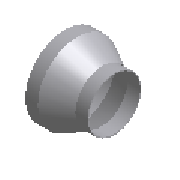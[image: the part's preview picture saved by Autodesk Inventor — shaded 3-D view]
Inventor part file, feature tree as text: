
AUTODESK INVENTOR PART (.ipt)
format: ipt  version: 2024.2 (Build 282272000, 272)  size: 172,032 bytes
history: native  units: mm (DEFAULTED — no unit token found)
features: other x4, revolve x1
ambient origin geometry x8: Origin, YZ Plane, XZ Plane, XY Plane, X Axis, Y Axis, Z Axis, Center Point
bodies: Solid1 (feature_tree)
feature tree (5):
  revolve  "Revolution1"  [1 undecoded]
  other  "Work Axis1"
  other  "Work Point1"
  other  "Work Axis2"
  other  "Work Point2"
note: 1 required parameter value undecoded (feature->parameter linkage not recoverable at this tier; creation-order binding heuristic only, values carry confidence <= 0.55)
